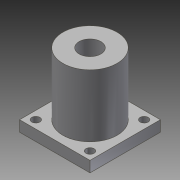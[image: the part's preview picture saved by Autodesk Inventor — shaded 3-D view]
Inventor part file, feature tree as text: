
AUTODESK INVENTOR PART (.ipt)
format: ipt  version: 2014 SP1 (Build 180222100, 222)  size: 110,080 bytes
history: native  units: in
note: dims shown in document units (in); Inventor stores cm internally (conversion verified against a paired STEP export)
features: extrude x3, sketch x3
ambient origin geometry x8: Origin, YZ Plane, XZ Plane, XY Plane, X Axis, Y Axis, Z Axis, Center Point
bodies: Solid1 (feature_tree)
feature tree (6):
  extrude  "Extrusion1"  Depth=1.625in
  extrude  "Extrusion2"  Depth=0.25in
  extrude  "Extrusion3"  Depth=1.4375in TaperAngle=0.0deg
  sketch  "Sketch1"  dims[d0=1.625in d1=1.625in]
  sketch  "Sketch2"  dims[d2=0.25in d3=0.0in d4=0.5in]
  sketch  "Sketch3"  dims[d5=1.25in d6=1.4375in d7=0.0in d8=0.1875in d10=1.25in d11=0.625in d12=0.625in d13=1.4375in d14=0.0in d15=0.5in]
